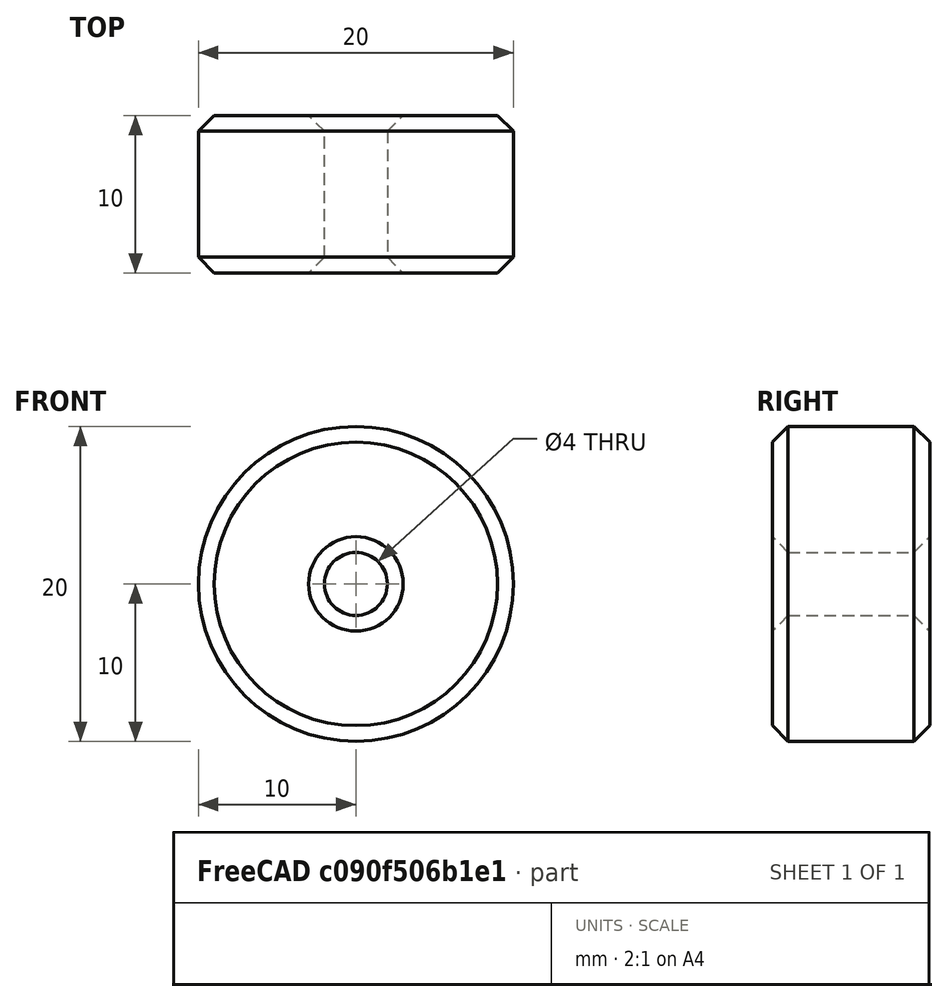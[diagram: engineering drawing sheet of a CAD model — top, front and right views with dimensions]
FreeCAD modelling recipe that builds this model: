
FCSTD DOCUMENT  (FreeCAD 1.1R38871 (Git))
Label: HoleTest
License: All rights reserved
LicenseURL: https://en.wikipedia.org/wiki/All_rights_reserved
objects: Sketcher::SketchObject×1, PartDesign::Pad×1, PartDesign::Chamfer×1, PartDesign::Body×1
note: 9 computed .brp shape members not serialized (recipe doc carries the construction recipe); baked Part::Feature solids carry a one-line shape summary decoded from their .brp

FEATURE [Sketcher::SketchObject] Sketch
  ArcFitTolerance = 1e-06
  AttachmentSupport = -> [XZ_Plane]
  FullyConstrained = true
  MakeInternals = false
  MapMode = 5
  Placement = pos=(0,0,0) rot=(1,0,0;1.5708rad)
  sketch-geometry (2):
    g0: Circle CenterX=0 CenterY=0 CenterZ=0 NormalX=0 NormalY=0 NormalZ=1 AngleXU=0 Radius=2
    g1: Circle CenterX=0 CenterY=0 CenterZ=0 NormalX=0 NormalY=0 NormalZ=1 AngleXU=0 Radius=10
  constraints (4):
    c: Diameter(g0) = 4
    c: Coincident(g0,g-1)
    c: Diameter(g1) = 20
    c: Coincident(g1,g0)
FEATURE [PartDesign::Pad] Pad
  Direction = (0,-1,2e-16)
  Length = 10
  Length2 = 10
  Placement = pos=(0,0,0) rot=(1,0,0;1.5708rad)
  Profile = -> Sketch
  ReferenceAxis = -> Sketch [N_Axis]
  Refine = true
  Suppressed = false
  Type = 0
FEATURE [PartDesign::Chamfer] Chamfer
  Angle = 45
  Base = -> Pad [Edge6,Edge5,Edge3,Edge2]
  BaseFeature = -> Pad
  ChamferType = 0
  FlipDirection = false
  Placement = pos=(0,0,0) rot=(1,0,0;1.5708rad)
  Refine = true
  Size = 1
  Size2 = 1
  SupportTransform = false
  Suppressed = false
  UseAllEdges = false
FEATURE [PartDesign::Body] Body
  AllowCompound = false
  Group = -> [Sketch,Pad,Chamfer]
  Origin = -> Origin
  Tip = -> Chamfer
